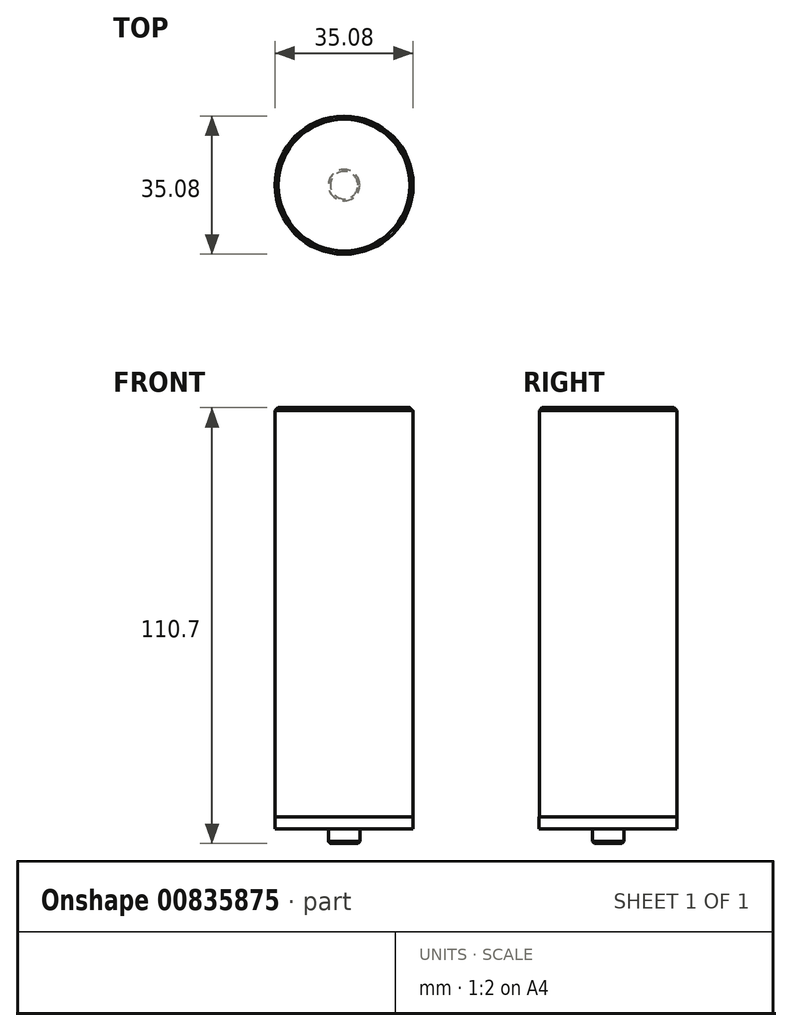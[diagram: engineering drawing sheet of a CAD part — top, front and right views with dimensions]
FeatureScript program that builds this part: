
annotation { "Feature Type Name" : "Feature", "Feature Type Description" : "" }
export const myFeature = defineFeature(function(context is Context, id is Id, definition is map)
    precondition{}
    {
        {
            var Q0;
            Q0=qCreatedBy(makeId("Top.planeOp"),FACE);
            var sketch = newSketch(context, id + "F0", { "sketchPlane" : qUnion([Q0])});
            skLineSegment(sketch, "E0", {"start": v(1927.03, -337.54) * mm, "end": v(1927.03, -469.7) * mm});
            skLineSegment(sketch, "E1", {"start": v(1927.03, -469.7) * mm, "end": v(1927.03, -337.54) * mm});
            skLineSegment(sketch, "E2", {"start": v(287.54, -421.48) * mm, "end": v(287.54, -466.13) * mm});
            skLineSegment(sketch, "E3", {"start": v(287.54, -466.13) * mm, "end": v(287.54, -421.48) * mm});
            skLineSegment(sketch, "E4", {"start": v(1069.78, -357.19) * mm, "end": v(1069.78, -466.13) * mm});
            skLineSegment(sketch, "E5", {"start": v(1069.78, -466.13) * mm, "end": v(1069.78, -357.19) * mm});
            skLineSegment(sketch, "E6", {"start": v(19.65, -350.04) * mm, "end": v(19.65, -466.13) * mm});
            skLineSegment(sketch, "E7", {"start": v(19.65, -466.13) * mm, "end": v(19.65, -350.04) * mm});
            skFitSpline(sketch, "E8", {"points": [v(1927.03, -469.7) * mm, v(1678.19, -799.5) * mm, v(1475.78, -964.4) * mm, v(1319.8, -964.4) * mm]});
            skFitSpline(sketch, "E9", {"points": [v(1319.8, -964.4) * mm, v(1235.27, -964.4) * mm, v(1168.6, -918.57) * mm, v(1119.78, -826.89) * mm]});
            skFitSpline(sketch, "E10", {"points": [v(1119.78, -826.89) * mm, v(1072.16, -734.02) * mm, v(1048.35, -612.58) * mm, v(1048.35, -462.56) * mm]});
            skFitSpline(sketch, "E11", {"points": [v(1048.35, -462.56) * mm, v(1048.35, -341.11) * mm, v(1076.92, -197.05) * mm, v(1134.07, -30.36) * mm]});
            skFitSpline(sketch, "E12", {"points": [v(1134.07, -30.36) * mm, v(1191.22, 137.52) * mm, v(1267.42, 307.18) * mm, v(1362.67, 478.63) * mm]});
            skFitSpline(sketch, "E13", {"points": [v(1362.67, 478.63) * mm, v(1459.11, 651.27) * mm, v(1558.53, 801.3) * mm, v(1660.92, 928.69) * mm]});
            skFitSpline(sketch, "E14", {"points": [v(1660.92, 928.69) * mm, v(1764.5, 1057.28) * mm, v(1860.35, 1147.17) * mm, v(1948.46, 1198.36) * mm]});
            skFitSpline(sketch, "E15", {"points": [v(1948.46, 1198.36) * mm, v(1984.18, 1219.8) * mm, v(2012.16, 1230.51) * mm, v(2032.4, 1230.51) * mm]});
            skFitSpline(sketch, "E16", {"points": [v(2032.4, 1230.51) * mm, v(2057.4, 1230.51) * mm, v(2074.07, 1219.2) * mm, v(2082.4, 1196.58) * mm]});
            skFitSpline(sketch, "E17", {"points": [v(2082.4, 1196.58) * mm, v(2090.74, 1175.15) * mm, v(2094.9, 1137.64) * mm, v(2094.9, 1084.06) * mm]});
            skFitSpline(sketch, "E18", {"points": [v(2094.9, 1084.06) * mm, v(2094.9, 918.57) * mm, v(2027.63, 714.97) * mm, v(1893.1, 473.27) * mm]});
            skFitSpline(sketch, "E19", {"points": [v(1893.1, 473.27) * mm, v(1758.55, 232.77) * mm, v(1571.03, -13.1) * mm, v(1330.52, -264.32) * mm]});
            skFitSpline(sketch, "E20", {"points": [v(1330.52, -264.32) * mm, v(1318.62, -326.23) * mm, v(1312.66, -373.86) * mm, v(1312.66, -407.2) * mm]});
            skFitSpline(sketch, "E21", {"points": [v(1312.66, -407.2) * mm, v(1312.66, -483.4) * mm, v(1328.74, -545.3) * mm, v(1360.88, -592.93) * mm]});
            skFitSpline(sketch, "E22", {"points": [v(1360.88, -592.93) * mm, v(1394.22, -640.56) * mm, v(1440.06, -664.37) * mm, v(1498.4, -664.37) * mm]});
            skFitSpline(sketch, "E23", {"points": [v(1498.4, -664.37) * mm, v(1528.17, -664.37) * mm, v(1560.31, -653.06) * mm, v(1594.84, -630.44) * mm]});
            skFitSpline(sketch, "E24", {"points": [v(1594.84, -630.44) * mm, v(1629.37, -606.62) * mm, v(1665.68, -577.45) * mm, v(1703.78, -542.92) * mm]});
            skFitSpline(sketch, "E25", {"points": [v(1703.78, -542.92) * mm, v(1741.88, -508.4) * mm, v(1816.3, -439.94) * mm, v(1927.03, -337.54) * mm]});
            skFitSpline(sketch, "E26", {"points": [v(1393.03, -16.07) * mm, v(1454.94, 44.65) * mm, v(1514.48, 113.7) * mm, v(1571.63, 191.1) * mm]});
            skFitSpline(sketch, "E27", {"points": [v(1571.63, 191.1) * mm, v(1629.97, 268.49) * mm, v(1684.73, 351.23) * mm, v(1735.93, 439.34) * mm]});
            skFitSpline(sketch, "E28", {"points": [v(1735.93, 439.34) * mm, v(1787.13, 527.45) * mm, v(1827.01, 606.62) * mm, v(1855.59, 676.87) * mm]});
            skFitSpline(sketch, "E29", {"points": [v(1855.59, 676.87) * mm, v(1885.35, 747.12) * mm, v(1900.24, 800.1) * mm, v(1900.24, 835.82) * mm]});
            skFitSpline(sketch, "E30", {"points": [v(1900.24, 835.82) * mm, v(1900.24, 863.2) * mm, v(1890.71, 876.9) * mm, v(1871.66, 876.9) * mm]});
            skFitSpline(sketch, "E31", {"points": [v(1871.66, 876.9) * mm, v(1864.52, 876.9) * mm, v(1850.83, 870.35) * mm, v(1830.59, 857.25) * mm]});
            skFitSpline(sketch, "E32", {"points": [v(1830.59, 857.25) * mm, v(1757.96, 797.72) * mm, v(1676.4, 681.04) * mm, v(1585.91, 507.2) * mm]});
            skFitSpline(sketch, "E33", {"points": [v(1585.91, 507.2) * mm, v(1495.42, 334.57) * mm, v(1431.13, 160.14) * mm, v(1393.03, -16.07) * mm]});
            skFitSpline(sketch, "E34", {"points": [v(287.54, -466.13) * mm, v(287.54, -536.38) * mm, v(304.8, -591.15) * mm, v(339.33, -630.44) * mm]});
            skFitSpline(sketch, "E35", {"points": [v(339.33, -630.44) * mm, v(373.86, -669.73) * mm, v(419.1, -689.37) * mm, v(475.06, -689.37) * mm]});
            skFitSpline(sketch, "E36", {"points": [v(475.06, -689.37) * mm, v(533.4, -689.37) * mm, v(593.53, -675.68) * mm, v(655.44, -648.3) * mm]});
            skFitSpline(sketch, "E37", {"points": [v(655.44, -648.3) * mm, v(718.54, -620.91) * mm, v(781.05, -584.6) * mm, v(842.96, -539.35) * mm]});
            skFitSpline(sketch, "E38", {"points": [v(842.96, -539.35) * mm, v(904.87, -494.1) * mm, v(980.48, -433.39) * mm, v(1069.78, -357.19) * mm]});
            skFitSpline(sketch, "E39", {"points": [v(1069.78, -466.13) * mm, v(935.24, -628.05) * mm, v(809.03, -752.47) * mm, v(691.16, -839.4) * mm]});
            skFitSpline(sketch, "E40", {"points": [v(691.16, -839.4) * mm, v(573.29, -925.12) * mm, v(453.63, -967.98) * mm, v(332.18, -967.98) * mm]});
            skFitSpline(sketch, "E41", {"points": [v(332.18, -967.98) * mm, v(226.22, -967.98) * mm, v(142.28, -926.9) * mm, v(80.37, -844.75) * mm]});
            skFitSpline(sketch, "E42", {"points": [v(80.37, -844.75) * mm, v(18.45, -762.6) * mm, v(-12.5, -650.08) * mm, v(-12.5, -507.2) * mm]});
            skFitSpline(sketch, "E43", {"points": [v(-12.5, -507.2) * mm, v(-12.5, -382.2) * mm, v(16.67, -269.08) * mm, v(75, -167.88) * mm]});
            skFitSpline(sketch, "E44", {"points": [v(75, -167.88) * mm, v(133.35, -65.48) * mm, v(228.6, 42.27) * mm, v(360.76, 155.38) * mm]});
            skFitSpline(sketch, "E45", {"points": [v(360.76, 155.38) * mm, v(451.25, 232.77) * mm, v(541.14, 291.1) * mm, v(630.44, 330.4) * mm]});
            skFitSpline(sketch, "E46", {"points": [v(630.44, 330.4) * mm, v(719.73, 369.69) * mm, v(799.5, 389.33) * mm, v(869.75, 389.33) * mm]});
            skFitSpline(sketch, "E47", {"points": [v(869.75, 389.33) * mm, v(925.71, 389.33) * mm, v(969.76, 376.24) * mm, v(1001.91, 350.04) * mm]});
            skFitSpline(sketch, "E48", {"points": [v(1001.91, 350.04) * mm, v(1035.25, 325.04) * mm, v(1051.92, 286.94) * mm, v(1051.92, 235.74) * mm]});
            skFitSpline(sketch, "E49", {"points": [v(1051.92, 235.74) * mm, v(1051.92, 160.73) * mm, v(1023.94, 85.73) * mm, v(967.98, 10.72) * mm]});
            skFitSpline(sketch, "E50", {"points": [v(967.98, 10.72) * mm, v(912.02, -63.1) * mm, v(826.3, -136.92) * mm, v(710.8, -210.74) * mm]});
            skFitSpline(sketch, "E51", {"points": [v(710.8, -210.74) * mm, v(596.5, -283.37) * mm, v(455.41, -353.62) * mm, v(287.54, -421.48) * mm]});
            skFitSpline(sketch, "E52", {"points": [v(305.4, -305.4) * mm, v(412.55, -263.72) * mm, v(504.23, -211.93) * mm, v(580.43, -150.02) * mm]});
            skFitSpline(sketch, "E53", {"points": [v(580.43, -150.02) * mm, v(656.63, -88.1) * mm, v(712.59, -29.17) * mm, v(748.3, 26.79) * mm]});
            skFitSpline(sketch, "E54", {"points": [v(748.3, 26.79) * mm, v(785.22, 83.94) * mm, v(803.67, 125.61) * mm, v(803.67, 151.8) * mm]});
            skFitSpline(sketch, "E55", {"points": [v(803.67, 151.8) * mm, v(803.67, 179.19) * mm, v(791.17, 192.88) * mm, v(766.17, 192.88) * mm]});
            skFitSpline(sketch, "E56", {"points": [v(766.17, 192.88) * mm, v(744.74, 192.88) * mm, v(709.61, 179.19) * mm, v(660.8, 151.8) * mm]});
            skFitSpline(sketch, "E57", {"points": [v(660.8, 151.8) * mm, v(613.17, 124.42) * mm, v(564.36, 88.7) * mm, v(514.35, 44.65) * mm]});
            skFitSpline(sketch, "E58", {"points": [v(514.35, 44.65) * mm, v(465.53, 0.6) * mm, v(421.48, -51.2) * mm, v(382.2, -110.73) * mm]});
            skFitSpline(sketch, "E59", {"points": [v(382.2, -110.73) * mm, v(342.9, -170.26) * mm, v(317.3, -235.15) * mm, v(305.4, -305.4) * mm]});
            skFitSpline(sketch, "E60", {"points": [v(19.65, -466.13) * mm, v(-180.38, -688.78) * mm, v(-364.33, -872.13) * mm, v(-532.2, -1016.2) * mm]});
            skFitSpline(sketch, "E61", {"points": [v(-532.2, -1016.2) * mm, v(-698.9, -1161.45) * mm, v(-862.01, -1272.78) * mm, v(-1021.56, -1350.17) * mm]});
            skFitSpline(sketch, "E62", {"points": [v(-1021.56, -1350.17) * mm, v(-1181.1, -1428.75) * mm, v(-1335.29, -1468.04) * mm, v(-1484.11, -1468.04) * mm]});
            skFitSpline(sketch, "E63", {"points": [v(-1484.11, -1468.04) * mm, v(-1612.7, -1468.04) * mm, v(-1723.43, -1442.44) * mm, v(-1816.3, -1391.25) * mm]});
            skFitSpline(sketch, "E64", {"points": [v(-1816.3, -1391.25) * mm, v(-1907.98, -1340.05) * mm, v(-1977.63, -1265.04) * mm, v(-2025.25, -1166.22) * mm]});
            skFitSpline(sketch, "E65", {"points": [v(-2025.25, -1166.22) * mm, v(-2071.69, -1068.59) * mm, v(-2094.9, -952.5) * mm, v(-2094.9, -817.96) * mm]});
            skFitSpline(sketch, "E66", {"points": [v(-2094.9, -817.96) * mm, v(-2094.9, -712) * mm, v(-2078.24, -600.07) * mm, v(-2044.9, -482.2) * mm]});
            skFitSpline(sketch, "E67", {"points": [v(-2044.9, -482.2) * mm, v(-2010.37, -363.14) * mm, v(-1960.96, -243.48) * mm, v(-1896.67, -123.23) * mm]});
            skFitSpline(sketch, "E68", {"points": [v(-1896.67, -123.23) * mm, v(-1832.37, -1.79) * mm, v(-1753.8, 123.23) * mm, v(-1660.92, 251.82) * mm]});
            skFitSpline(sketch, "E69", {"points": [v(-1660.92, 251.82) * mm, v(-1566.86, 380.4) * mm, v(-1456.73, 515.54) * mm, v(-1330.52, 657.23) * mm]});
            skFitSpline(sketch, "E70", {"points": [v(-1330.52, 657.23) * mm, v(-1199.55, 803.67) * mm, v(-1070.37, 929.88) * mm, v(-942.97, 1035.84) * mm]});
            skFitSpline(sketch, "E71", {"points": [v(-942.97, 1035.84) * mm, v(-815.58, 1143) * mm, v(-700.09, 1226.94) * mm, v(-596.5, 1287.66) * mm]});
            skFitSpline(sketch, "E72", {"points": [v(-596.5, 1287.66) * mm, v(-492.92, 1348.38) * mm, v(-397.07, 1393.63) * mm, v(-308.97, 1423.4) * mm]});
            skFitSpline(sketch, "E73", {"points": [v(-308.97, 1423.4) * mm, v(-219.67, 1453.16) * mm, v(-145.85, 1468.04) * mm, v(-87.51, 1468.04) * mm]});
            skFitSpline(sketch, "E74", {"points": [v(-87.51, 1468.04) * mm, v(-27.98, 1468.04) * mm, v(22.62, 1453.75) * mm, v(64.3, 1425.18) * mm]});
            skFitSpline(sketch, "E75", {"points": [v(64.3, 1425.18) * mm, v(105.97, 1396.6) * mm, v(138.11, 1354.93) * mm, v(160.73, 1300.16) * mm]});
            skFitSpline(sketch, "E76", {"points": [v(160.73, 1300.16) * mm, v(183.36, 1245.4) * mm, v(194.67, 1182.3) * mm, v(194.67, 1110.85) * mm]});
            skFitSpline(sketch, "E77", {"points": [v(194.67, 1110.85) * mm, v(194.67, 976.31) * mm, v(148.83, 826.3) * mm, v(57.15, 660.8) * mm]});
            skFitSpline(sketch, "E78", {"points": [v(57.15, 660.8) * mm, v(-34.53, 496.5) * mm, v(-148.83, 337.54) * mm, v(-285.75, 183.95) * mm]});
            skFitSpline(sketch, "E79", {"points": [v(-285.75, 183.95) * mm, v(-422.67, 30.36) * mm, v(-553.64, -95.25) * mm, v(-678.66, -192.88) * mm]});
            skFitSpline(sketch, "E80", {"points": [v(-678.66, -192.88) * mm, v(-802.48, -289.32) * mm, v(-891.78, -337.54) * mm, v(-946.55, -337.54) * mm]});
            skFitSpline(sketch, "E81", {"points": [v(-946.55, -337.54) * mm, v(-983.46, -337.54) * mm, v(-1017.98, -323.25) * mm, v(-1050.13, -294.68) * mm]});
            skFitSpline(sketch, "E82", {"points": [v(-1050.13, -294.68) * mm, v(-1081.09, -264.91) * mm, v(-1096.57, -231.58) * mm, v(-1096.57, -194.67) * mm]});
            skFitSpline(sketch, "E83", {"points": [v(-1096.57, -194.67) * mm, v(-1096.57, -126.8) * mm, v(-1060.85, -44.65) * mm, v(-989.4, 51.8) * mm]});
            skFitSpline(sketch, "E84", {"points": [v(-989.4, 51.8) * mm, v(-916.78, 148.23) * mm, v(-838.2, 236.34) * mm, v(-753.67, 316.11) * mm]});
            skFitSpline(sketch, "E85", {"points": [v(-753.67, 316.11) * mm, v(-667.94, 397.07) * mm, v(-616.74, 437.55) * mm, v(-600.07, 437.55) * mm]});
            skFitSpline(sketch, "E86", {"points": [v(-600.07, 437.55) * mm, v(-591.74, 437.55) * mm, v(-587.57, 433.98) * mm, v(-587.57, 426.84) * mm]});
            skFitSpline(sketch, "E87", {"points": [v(-587.57, 426.84) * mm, v(-587.57, 416.12) * mm, v(-594.12, 397.67) * mm, v(-607.22, 371.48) * mm]});
            skFitSpline(sketch, "E88", {"points": [v(-607.22, 371.48) * mm, v(-619.12, 345.28) * mm, v(-625.08, 329.2) * mm, v(-625.08, 323.25) * mm]});
            skFitSpline(sketch, "E89", {"points": [v(-625.08, 323.25) * mm, v(-625.08, 313.73) * mm, v(-621.5, 308.97) * mm, v(-614.36, 308.97) * mm]});
            skFitSpline(sketch, "E90", {"points": [v(-614.36, 308.97) * mm, v(-594.12, 308.97) * mm, v(-535.78, 363.14) * mm, v(-439.34, 471.49) * mm]});
            skFitSpline(sketch, "E91", {"points": [v(-439.34, 471.49) * mm, v(-342.9, 579.83) * mm, v(-254.8, 698.9) * mm, v(-175.02, 828.68) * mm]});
            skFitSpline(sketch, "E92", {"points": [v(-175.02, 828.68) * mm, v(-94.06, 959.64) * mm, v(-53.58, 1066.8) * mm, v(-53.58, 1150.14) * mm]});
            skFitSpline(sketch, "E93", {"points": [v(-53.58, 1150.14) * mm, v(-53.58, 1184.67) * mm, v(-61.32, 1210.87) * mm, v(-76.8, 1228.73) * mm]});
            skFitSpline(sketch, "E94", {"points": [v(-76.8, 1228.73) * mm, v(-91.08, 1247.78) * mm, v(-113.1, 1257.3) * mm, v(-142.87, 1257.3) * mm]});
            skFitSpline(sketch, "E95", {"points": [v(-142.87, 1257.3) * mm, v(-226.22, 1257.3) * mm, v(-353.02, 1189.43) * mm, v(-523.28, 1053.7) * mm]});
            skFitSpline(sketch, "E96", {"points": [v(-523.28, 1053.7) * mm, v(-692.35, 919.16) * mm, v(-866.18, 747.12) * mm, v(-1044.77, 537.57) * mm]});
            skFitSpline(sketch, "E97", {"points": [v(-1044.77, 537.57) * mm, v(-1222.18, 329.2) * mm, v(-1370.4, 113.7) * mm, v(-1489.47, -108.94) * mm]});
            skFitSpline(sketch, "E98", {"points": [v(-1489.47, -108.94) * mm, v(-1608.53, -331.59) * mm, v(-1668.07, -527.45) * mm, v(-1668.07, -696.52) * mm]});
            skFitSpline(sketch, "E99", {"points": [v(-1668.07, -696.52) * mm, v(-1668.07, -794.15) * mm, v(-1653.78, -875.7) * mm, v(-1625.2, -941.19) * mm]});
            skFitSpline(sketch, "E100", {"points": [v(-1625.2, -941.19) * mm, v(-1595.44, -1006.67) * mm, v(-1552.58, -1057.27) * mm, v(-1496.62, -1093) * mm]});
            skFitSpline(sketch, "E101", {"points": [v(-1496.62, -1093) * mm, v(-1439.47, -1128.71) * mm, v(-1371, -1146.57) * mm, v(-1291.23, -1146.57) * mm]});
            skFitSpline(sketch, "E102", {"points": [v(-1291.23, -1146.57) * mm, v(-1118.6, -1146.57) * mm, v(-922.73, -1079.3) * mm, v(-703.66, -944.76) * mm]});
            skFitSpline(sketch, "E103", {"points": [v(-703.66, -944.76) * mm, v(-484.58, -810.22) * mm, v(-243.48, -611.98) * mm, v(19.65, -350.04) * mm]});
            skSolve(sketch);
        }
        {
            var Q0;
            Q0 = qSketchRegion(id + "F0", true);
            extrude(context, id + "F1", {"entities" : qUnion([Q0]), "depth" : 160 * mm, "offsetDistance" : 25.4 * mm});
        }
        {
            var Q0;
            Q0=makeQuery(id+"F1.opExtrude","SWEPT_BODY",BODY,{"disambiguationData":[OSD([sQuery(id+"F0.wireOp",EDGE,"E1"),sQuery(id+"F0.wireOp",EDGE,"E3"),sQuery(id+"F0.wireOp",EDGE,"E8"),sQuery(id+"F0.wireOp",EDGE,"E9"),sQuery(id+"F0.wireOp",EDGE,"E10"),sQuery(id+"F0.wireOp",EDGE,"E11"),sQuery(id+"F0.wireOp",EDGE,"E12"),sQuery(id+"F0.wireOp",EDGE,"E13"),sQuery(id+"F0.wireOp",EDGE,"E14"),sQuery(id+"F0.wireOp",EDGE,"E15"),sQuery(id+"F0.wireOp",EDGE,"E16"),sQuery(id+"F0.wireOp",EDGE,"E17"),sQuery(id+"F0.wireOp",EDGE,"E18"),sQuery(id+"F0.wireOp",EDGE,"E19"),sQuery(id+"F0.wireOp",EDGE,"E20"),sQuery(id+"F0.wireOp",EDGE,"E21"),sQuery(id+"F0.wireOp",EDGE,"E22"),sQuery(id+"F0.wireOp",EDGE,"E23"),sQuery(id+"F0.wireOp",EDGE,"E24"),sQuery(id+"F0.wireOp",EDGE,"E25"),sQuery(id+"F0.wireOp",EDGE,"E26"),sQuery(id+"F0.wireOp",EDGE,"E27"),sQuery(id+"F0.wireOp",EDGE,"E28"),sQuery(id+"F0.wireOp",EDGE,"E29"),sQuery(id+"F0.wireOp",EDGE,"E30"),sQuery(id+"F0.wireOp",EDGE,"E31"),sQuery(id+"F0.wireOp",EDGE,"E32"),sQuery(id+"F0.wireOp",EDGE,"E33"),sQuery(id+"F0.wireOp",EDGE,"E34"),sQuery(id+"F0.wireOp",EDGE,"E35"),sQuery(id+"F0.wireOp",EDGE,"E36"),sQuery(id+"F0.wireOp",EDGE,"E37"),sQuery(id+"F0.wireOp",EDGE,"E38"),sQuery(id+"F0.wireOp",EDGE,"E39"),sQuery(id+"F0.wireOp",EDGE,"E40"),sQuery(id+"F0.wireOp",EDGE,"E41"),sQuery(id+"F0.wireOp",EDGE,"E42"),sQuery(id+"F0.wireOp",EDGE,"E43"),sQuery(id+"F0.wireOp",EDGE,"E44"),sQuery(id+"F0.wireOp",EDGE,"E45"),sQuery(id+"F0.wireOp",EDGE,"E46"),sQuery(id+"F0.wireOp",EDGE,"E47"),sQuery(id+"F0.wireOp",EDGE,"E48"),sQuery(id+"F0.wireOp",EDGE,"E49"),sQuery(id+"F0.wireOp",EDGE,"E50"),sQuery(id+"F0.wireOp",EDGE,"E51"),sQuery(id+"F0.wireOp",EDGE,"E52"),sQuery(id+"F0.wireOp",EDGE,"E53"),sQuery(id+"F0.wireOp",EDGE,"E54"),sQuery(id+"F0.wireOp",EDGE,"E55"),sQuery(id+"F0.wireOp",EDGE,"E56"),sQuery(id+"F0.wireOp",EDGE,"E57"),sQuery(id+"F0.wireOp",EDGE,"E58"),sQuery(id+"F0.wireOp",EDGE,"E59"),sQuery(id+"F0.wireOp",EDGE,"E60"),sQuery(id+"F0.wireOp",EDGE,"E61"),sQuery(id+"F0.wireOp",EDGE,"E62"),sQuery(id+"F0.wireOp",EDGE,"E63"),sQuery(id+"F0.wireOp",EDGE,"E64"),sQuery(id+"F0.wireOp",EDGE,"E65"),sQuery(id+"F0.wireOp",EDGE,"E66"),sQuery(id+"F0.wireOp",EDGE,"E67"),sQuery(id+"F0.wireOp",EDGE,"E68"),sQuery(id+"F0.wireOp",EDGE,"E69"),sQuery(id+"F0.wireOp",EDGE,"E70"),sQuery(id+"F0.wireOp",EDGE,"E71"),sQuery(id+"F0.wireOp",EDGE,"E72"),sQuery(id+"F0.wireOp",EDGE,"E73"),sQuery(id+"F0.wireOp",EDGE,"E74"),sQuery(id+"F0.wireOp",EDGE,"E75"),sQuery(id+"F0.wireOp",EDGE,"E76"),sQuery(id+"F0.wireOp",EDGE,"E77"),sQuery(id+"F0.wireOp",EDGE,"E78"),sQuery(id+"F0.wireOp",EDGE,"E79"),sQuery(id+"F0.wireOp",EDGE,"E80"),sQuery(id+"F0.wireOp",EDGE,"E81"),sQuery(id+"F0.wireOp",EDGE,"E82"),sQuery(id+"F0.wireOp",EDGE,"E83"),sQuery(id+"F0.wireOp",EDGE,"E84"),sQuery(id+"F0.wireOp",EDGE,"E85"),sQuery(id+"F0.wireOp",EDGE,"E86"),sQuery(id+"F0.wireOp",EDGE,"E87"),sQuery(id+"F0.wireOp",EDGE,"E88"),sQuery(id+"F0.wireOp",EDGE,"E89"),sQuery(id+"F0.wireOp",EDGE,"E90"),sQuery(id+"F0.wireOp",EDGE,"E91"),sQuery(id+"F0.wireOp",EDGE,"E92"),sQuery(id+"F0.wireOp",EDGE,"E93"),sQuery(id+"F0.wireOp",EDGE,"E94"),sQuery(id+"F0.wireOp",EDGE,"E95"),sQuery(id+"F0.wireOp",EDGE,"E96"),sQuery(id+"F0.wireOp",EDGE,"E97"),sQuery(id+"F0.wireOp",EDGE,"E98"),sQuery(id+"F0.wireOp",EDGE,"E99"),sQuery(id+"F0.wireOp",EDGE,"E100"),sQuery(id+"F0.wireOp",EDGE,"E101"),sQuery(id+"F0.wireOp",EDGE,"E102"),sQuery(id+"F0.wireOp",EDGE,"E103")])]});
            var Q1;
            Q1=qCreatedBy(makeId("Origin.pointOp"),VERTEX);
            transform(context, id + "F2", {"entities" : qUnion([Q0]), "transformType" : TransformType.SCALE_UNIFORMLY, "scale" : .65, "scalePoint" : qUnion([Q1]), "makeCopy" : false});
        }
        {
            var Q0;
            Q0=qCreatedBy(makeId("Top.planeOp"),FACE);
            var sketch = newSketch(context, id + "F3", { "sketchPlane" : qUnion([Q0])});
            skCircle(sketch, "E104", {"center": v(0, 0) * mm, "radius": 17.5 * mm});
            skSolve(sketch);
        }
        {
            var Q0;
            Q0=makeQuery(id+"F3.imprint","IMPRINT",FACE,{"disambiguationData":[TD([[makeQuery(id+"F3.imprint","IMPRINT",EDGE,{"derivedFrom":sQuery(id+"F3.wireOp",EDGE,"E104")}),1.0]])]});
            var Q1;
            Q1=makeQuery(id+"F1.opExtrude","CAP_FACE",FACE,{"disambiguationData":[OSD([sQuery(id+"F0.wireOp",EDGE,"E1"),sQuery(id+"F0.wireOp",EDGE,"E3"),sQuery(id+"F0.wireOp",EDGE,"E8"),sQuery(id+"F0.wireOp",EDGE,"E9"),sQuery(id+"F0.wireOp",EDGE,"E10"),sQuery(id+"F0.wireOp",EDGE,"E11"),sQuery(id+"F0.wireOp",EDGE,"E12"),sQuery(id+"F0.wireOp",EDGE,"E13"),sQuery(id+"F0.wireOp",EDGE,"E14"),sQuery(id+"F0.wireOp",EDGE,"E15"),sQuery(id+"F0.wireOp",EDGE,"E16"),sQuery(id+"F0.wireOp",EDGE,"E17"),sQuery(id+"F0.wireOp",EDGE,"E18"),sQuery(id+"F0.wireOp",EDGE,"E19"),sQuery(id+"F0.wireOp",EDGE,"E20"),sQuery(id+"F0.wireOp",EDGE,"E21"),sQuery(id+"F0.wireOp",EDGE,"E22"),sQuery(id+"F0.wireOp",EDGE,"E23"),sQuery(id+"F0.wireOp",EDGE,"E24"),sQuery(id+"F0.wireOp",EDGE,"E25"),sQuery(id+"F0.wireOp",EDGE,"E26"),sQuery(id+"F0.wireOp",EDGE,"E27"),sQuery(id+"F0.wireOp",EDGE,"E28"),sQuery(id+"F0.wireOp",EDGE,"E29"),sQuery(id+"F0.wireOp",EDGE,"E30"),sQuery(id+"F0.wireOp",EDGE,"E31"),sQuery(id+"F0.wireOp",EDGE,"E32"),sQuery(id+"F0.wireOp",EDGE,"E33"),sQuery(id+"F0.wireOp",EDGE,"E34"),sQuery(id+"F0.wireOp",EDGE,"E35"),sQuery(id+"F0.wireOp",EDGE,"E36"),sQuery(id+"F0.wireOp",EDGE,"E37"),sQuery(id+"F0.wireOp",EDGE,"E38"),sQuery(id+"F0.wireOp",EDGE,"E39"),sQuery(id+"F0.wireOp",EDGE,"E40"),sQuery(id+"F0.wireOp",EDGE,"E41"),sQuery(id+"F0.wireOp",EDGE,"E42"),sQuery(id+"F0.wireOp",EDGE,"E43"),sQuery(id+"F0.wireOp",EDGE,"E44"),sQuery(id+"F0.wireOp",EDGE,"E45"),sQuery(id+"F0.wireOp",EDGE,"E46"),sQuery(id+"F0.wireOp",EDGE,"E47"),sQuery(id+"F0.wireOp",EDGE,"E48"),sQuery(id+"F0.wireOp",EDGE,"E49"),sQuery(id+"F0.wireOp",EDGE,"E50"),sQuery(id+"F0.wireOp",EDGE,"E51"),sQuery(id+"F0.wireOp",EDGE,"E52"),sQuery(id+"F0.wireOp",EDGE,"E53"),sQuery(id+"F0.wireOp",EDGE,"E54"),sQuery(id+"F0.wireOp",EDGE,"E55"),sQuery(id+"F0.wireOp",EDGE,"E56"),sQuery(id+"F0.wireOp",EDGE,"E57"),sQuery(id+"F0.wireOp",EDGE,"E58"),sQuery(id+"F0.wireOp",EDGE,"E59"),sQuery(id+"F0.wireOp",EDGE,"E60"),sQuery(id+"F0.wireOp",EDGE,"E61"),sQuery(id+"F0.wireOp",EDGE,"E62"),sQuery(id+"F0.wireOp",EDGE,"E63"),sQuery(id+"F0.wireOp",EDGE,"E64"),sQuery(id+"F0.wireOp",EDGE,"E65"),sQuery(id+"F0.wireOp",EDGE,"E66"),sQuery(id+"F0.wireOp",EDGE,"E67"),sQuery(id+"F0.wireOp",EDGE,"E68"),sQuery(id+"F0.wireOp",EDGE,"E69"),sQuery(id+"F0.wireOp",EDGE,"E70"),sQuery(id+"F0.wireOp",EDGE,"E71"),sQuery(id+"F0.wireOp",EDGE,"E72"),sQuery(id+"F0.wireOp",EDGE,"E73"),sQuery(id+"F0.wireOp",EDGE,"E74"),sQuery(id+"F0.wireOp",EDGE,"E75"),sQuery(id+"F0.wireOp",EDGE,"E76"),sQuery(id+"F0.wireOp",EDGE,"E77"),sQuery(id+"F0.wireOp",EDGE,"E78"),sQuery(id+"F0.wireOp",EDGE,"E79"),sQuery(id+"F0.wireOp",EDGE,"E80"),sQuery(id+"F0.wireOp",EDGE,"E81"),sQuery(id+"F0.wireOp",EDGE,"E82"),sQuery(id+"F0.wireOp",EDGE,"E83"),sQuery(id+"F0.wireOp",EDGE,"E84"),sQuery(id+"F0.wireOp",EDGE,"E85"),sQuery(id+"F0.wireOp",EDGE,"E86"),sQuery(id+"F0.wireOp",EDGE,"E87"),sQuery(id+"F0.wireOp",EDGE,"E88"),sQuery(id+"F0.wireOp",EDGE,"E89"),sQuery(id+"F0.wireOp",EDGE,"E90"),sQuery(id+"F0.wireOp",EDGE,"E91"),sQuery(id+"F0.wireOp",EDGE,"E92"),sQuery(id+"F0.wireOp",EDGE,"E93"),sQuery(id+"F0.wireOp",EDGE,"E94"),sQuery(id+"F0.wireOp",EDGE,"E95"),sQuery(id+"F0.wireOp",EDGE,"E96"),sQuery(id+"F0.wireOp",EDGE,"E97"),sQuery(id+"F0.wireOp",EDGE,"E98"),sQuery(id+"F0.wireOp",EDGE,"E99"),sQuery(id+"F0.wireOp",EDGE,"E100"),sQuery(id+"F0.wireOp",EDGE,"E101"),sQuery(id+"F0.wireOp",EDGE,"E102"),sQuery(id+"F0.wireOp",EDGE,"E103")])],"isStart":false});
            extrude(context, id + "F4", {"entities" : qUnion([Q0]), "endBound" : BoundingType.UP_TO_SURFACE, "depth" : 25 * mm, "endBoundEntityFace" : qUnion([Q1]), "offsetDistance" : 25 * mm});
        }
        {
            var Q0;
            Q0=qCreatedBy(makeId("Top.planeOp"),FACE);
            var sketch = newSketch(context, id + "F5", { "sketchPlane" : qUnion([Q0])});
            skCircle(sketch, "E105", {"center": v(0, 0) * mm, "radius": 17.54 * mm});
            skSolve(sketch);
        }
        {
            var Q0;
            Q0 = qSketchRegion(id + "F5", true);
            extrude(context, id + "F6", {"entities" : qUnion([Q0]), "oppositeDirection" : true, "depth" : 3 * mm, "offsetDistance" : 25 * mm});
        }
        {
            var Q0;
            Q0=makeQuery(id+"F1.opExtrude","SWEPT_BODY",BODY,{"disambiguationData":[OSD([sQuery(id+"F0.wireOp",EDGE,"E1"),sQuery(id+"F0.wireOp",EDGE,"E3"),sQuery(id+"F0.wireOp",EDGE,"E8"),sQuery(id+"F0.wireOp",EDGE,"E9"),sQuery(id+"F0.wireOp",EDGE,"E10"),sQuery(id+"F0.wireOp",EDGE,"E11"),sQuery(id+"F0.wireOp",EDGE,"E12"),sQuery(id+"F0.wireOp",EDGE,"E13"),sQuery(id+"F0.wireOp",EDGE,"E14"),sQuery(id+"F0.wireOp",EDGE,"E15"),sQuery(id+"F0.wireOp",EDGE,"E16"),sQuery(id+"F0.wireOp",EDGE,"E17"),sQuery(id+"F0.wireOp",EDGE,"E18"),sQuery(id+"F0.wireOp",EDGE,"E19"),sQuery(id+"F0.wireOp",EDGE,"E20"),sQuery(id+"F0.wireOp",EDGE,"E21"),sQuery(id+"F0.wireOp",EDGE,"E22"),sQuery(id+"F0.wireOp",EDGE,"E23"),sQuery(id+"F0.wireOp",EDGE,"E24"),sQuery(id+"F0.wireOp",EDGE,"E25"),sQuery(id+"F0.wireOp",EDGE,"E26"),sQuery(id+"F0.wireOp",EDGE,"E27"),sQuery(id+"F0.wireOp",EDGE,"E28"),sQuery(id+"F0.wireOp",EDGE,"E29"),sQuery(id+"F0.wireOp",EDGE,"E30"),sQuery(id+"F0.wireOp",EDGE,"E31"),sQuery(id+"F0.wireOp",EDGE,"E32"),sQuery(id+"F0.wireOp",EDGE,"E33"),sQuery(id+"F0.wireOp",EDGE,"E34"),sQuery(id+"F0.wireOp",EDGE,"E35"),sQuery(id+"F0.wireOp",EDGE,"E36"),sQuery(id+"F0.wireOp",EDGE,"E37"),sQuery(id+"F0.wireOp",EDGE,"E38"),sQuery(id+"F0.wireOp",EDGE,"E39"),sQuery(id+"F0.wireOp",EDGE,"E40"),sQuery(id+"F0.wireOp",EDGE,"E41"),sQuery(id+"F0.wireOp",EDGE,"E42"),sQuery(id+"F0.wireOp",EDGE,"E43"),sQuery(id+"F0.wireOp",EDGE,"E44"),sQuery(id+"F0.wireOp",EDGE,"E45"),sQuery(id+"F0.wireOp",EDGE,"E46"),sQuery(id+"F0.wireOp",EDGE,"E47"),sQuery(id+"F0.wireOp",EDGE,"E48"),sQuery(id+"F0.wireOp",EDGE,"E49"),sQuery(id+"F0.wireOp",EDGE,"E50"),sQuery(id+"F0.wireOp",EDGE,"E51"),sQuery(id+"F0.wireOp",EDGE,"E52"),sQuery(id+"F0.wireOp",EDGE,"E53"),sQuery(id+"F0.wireOp",EDGE,"E54"),sQuery(id+"F0.wireOp",EDGE,"E55"),sQuery(id+"F0.wireOp",EDGE,"E56"),sQuery(id+"F0.wireOp",EDGE,"E57"),sQuery(id+"F0.wireOp",EDGE,"E58"),sQuery(id+"F0.wireOp",EDGE,"E59"),sQuery(id+"F0.wireOp",EDGE,"E60"),sQuery(id+"F0.wireOp",EDGE,"E61"),sQuery(id+"F0.wireOp",EDGE,"E62"),sQuery(id+"F0.wireOp",EDGE,"E63"),sQuery(id+"F0.wireOp",EDGE,"E64"),sQuery(id+"F0.wireOp",EDGE,"E65"),sQuery(id+"F0.wireOp",EDGE,"E66"),sQuery(id+"F0.wireOp",EDGE,"E67"),sQuery(id+"F0.wireOp",EDGE,"E68"),sQuery(id+"F0.wireOp",EDGE,"E69"),sQuery(id+"F0.wireOp",EDGE,"E70"),sQuery(id+"F0.wireOp",EDGE,"E71"),sQuery(id+"F0.wireOp",EDGE,"E72"),sQuery(id+"F0.wireOp",EDGE,"E73"),sQuery(id+"F0.wireOp",EDGE,"E74"),sQuery(id+"F0.wireOp",EDGE,"E75"),sQuery(id+"F0.wireOp",EDGE,"E76"),sQuery(id+"F0.wireOp",EDGE,"E77"),sQuery(id+"F0.wireOp",EDGE,"E78"),sQuery(id+"F0.wireOp",EDGE,"E79"),sQuery(id+"F0.wireOp",EDGE,"E80"),sQuery(id+"F0.wireOp",EDGE,"E81"),sQuery(id+"F0.wireOp",EDGE,"E82"),sQuery(id+"F0.wireOp",EDGE,"E83"),sQuery(id+"F0.wireOp",EDGE,"E84"),sQuery(id+"F0.wireOp",EDGE,"E85"),sQuery(id+"F0.wireOp",EDGE,"E86"),sQuery(id+"F0.wireOp",EDGE,"E87"),sQuery(id+"F0.wireOp",EDGE,"E88"),sQuery(id+"F0.wireOp",EDGE,"E89"),sQuery(id+"F0.wireOp",EDGE,"E90"),sQuery(id+"F0.wireOp",EDGE,"E91"),sQuery(id+"F0.wireOp",EDGE,"E92"),sQuery(id+"F0.wireOp",EDGE,"E93"),sQuery(id+"F0.wireOp",EDGE,"E94"),sQuery(id+"F0.wireOp",EDGE,"E95"),sQuery(id+"F0.wireOp",EDGE,"E96"),sQuery(id+"F0.wireOp",EDGE,"E97"),sQuery(id+"F0.wireOp",EDGE,"E98"),sQuery(id+"F0.wireOp",EDGE,"E99"),sQuery(id+"F0.wireOp",EDGE,"E100"),sQuery(id+"F0.wireOp",EDGE,"E101"),sQuery(id+"F0.wireOp",EDGE,"E102"),sQuery(id+"F0.wireOp",EDGE,"E103")])]});
            var Q1;
            Q1=makeQuery(id+"F4.opExtrude","SWEPT_BODY",BODY,{"disambiguationData":[OSD([sQuery(id+"F3.wireOp",EDGE,"E104")])]});
            booleanBodies(context, id + "F7", {"operationType" : BooleanOperationType.SUBTRACTION, "tools" : qUnion([Q0]), "targets" : qUnion([Q1])});
        }
        {
            var Q0;
            Q0=makeQuery(id+"F6.opExtrude","CAP_FACE",FACE,{"disambiguationData":[OSD([sQuery(id+"F5.wireOp",EDGE,"E105")])],"isStart":false});
            var sketch = newSketch(context, id + "F8", { "sketchPlane" : qUnion([Q0])});
            skCircle(sketch, "E106", {"center": v(0, 0) * mm, "radius": 4 * mm});
            skSolve(sketch);
        }
        {
            var Q0;
            Q0 = qSketchRegion(id + "F8", true);
            extrude(context, id + "F9", {"entities" : qUnion([Q0]), "operationType" : NewBodyOperationType.ADD, "depth" : 3.7 * mm, "offsetDistance" : 25 * mm});
        }
        {
            var Q0;
            Q0=makeQuery(id+"F9.opExtrude","CAP_EDGE",EDGE,{"disambiguationData":[OSD([sQuery(id+"F8.wireOp",EDGE,"E106")])],"isStart":false});
            chamfer(context, id + "F10", {"entities" : qUnion([Q0]), "width" : .5 * mm, "tangentPropagation" : true});
        }
        {
            var Q0;
            Q0=makeQuery(id+"F4.opExtrude","CAP_EDGE",EDGE,{"disambiguationData":[OSD([sQuery(id+"F3.wireOp",EDGE,"E104")])],"isStart":false});
            chamfer(context, id + "F11", {"entities" : qUnion([Q0]), "width" : .75 * mm, "tangentPropagation" : true});
        }
    });
